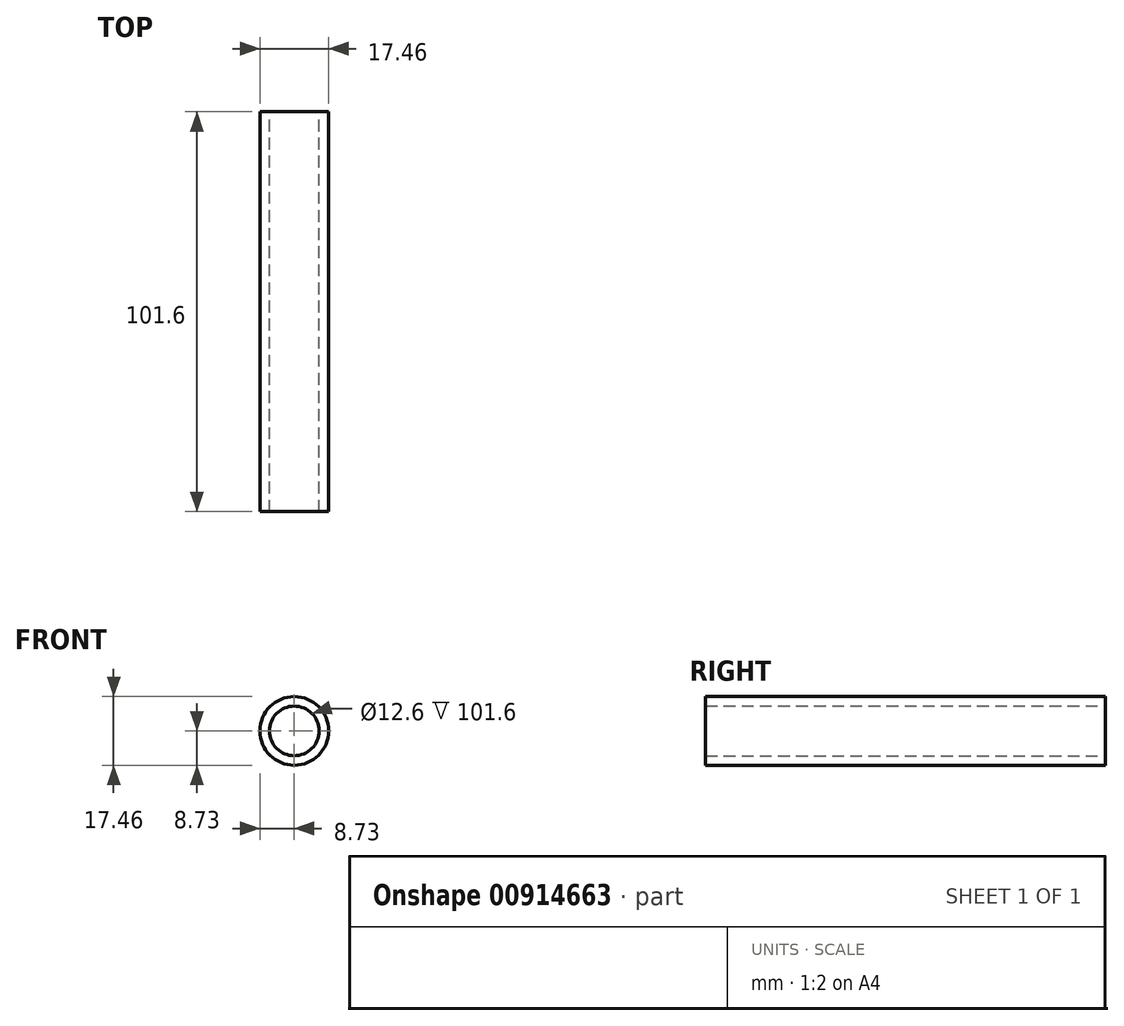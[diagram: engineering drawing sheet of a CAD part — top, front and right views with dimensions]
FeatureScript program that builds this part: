
annotation { "Feature Type Name" : "Feature", "Feature Type Description" : "" }
export const myFeature = defineFeature(function(context is Context, id is Id, definition is map)
    precondition{}
    {
        {
            var Q0;
            Q0=qCreatedBy(makeId("Front.planeOp"),FACE);
            var sketch = newSketch(context, id + "F0", { "sketchPlane" : qUnion([Q0])});
            skCircle(sketch, "E0", {"center": v(0, 0) * mm, "radius": 6.3 * mm});
            skCircle(sketch, "E1", {"center": v(0, 0) * mm, "radius": 8.73 * mm});
            skSolve(sketch);
        }
        {
            var Q0;
            Q0 = qSketchRegion(id + "F0", true);
            extrude(context, id + "F1", {"entities" : qUnion([Q0]), "depth" : 101.6 * mm, "offsetDistance" : 25.4 * mm});
        }
    });
